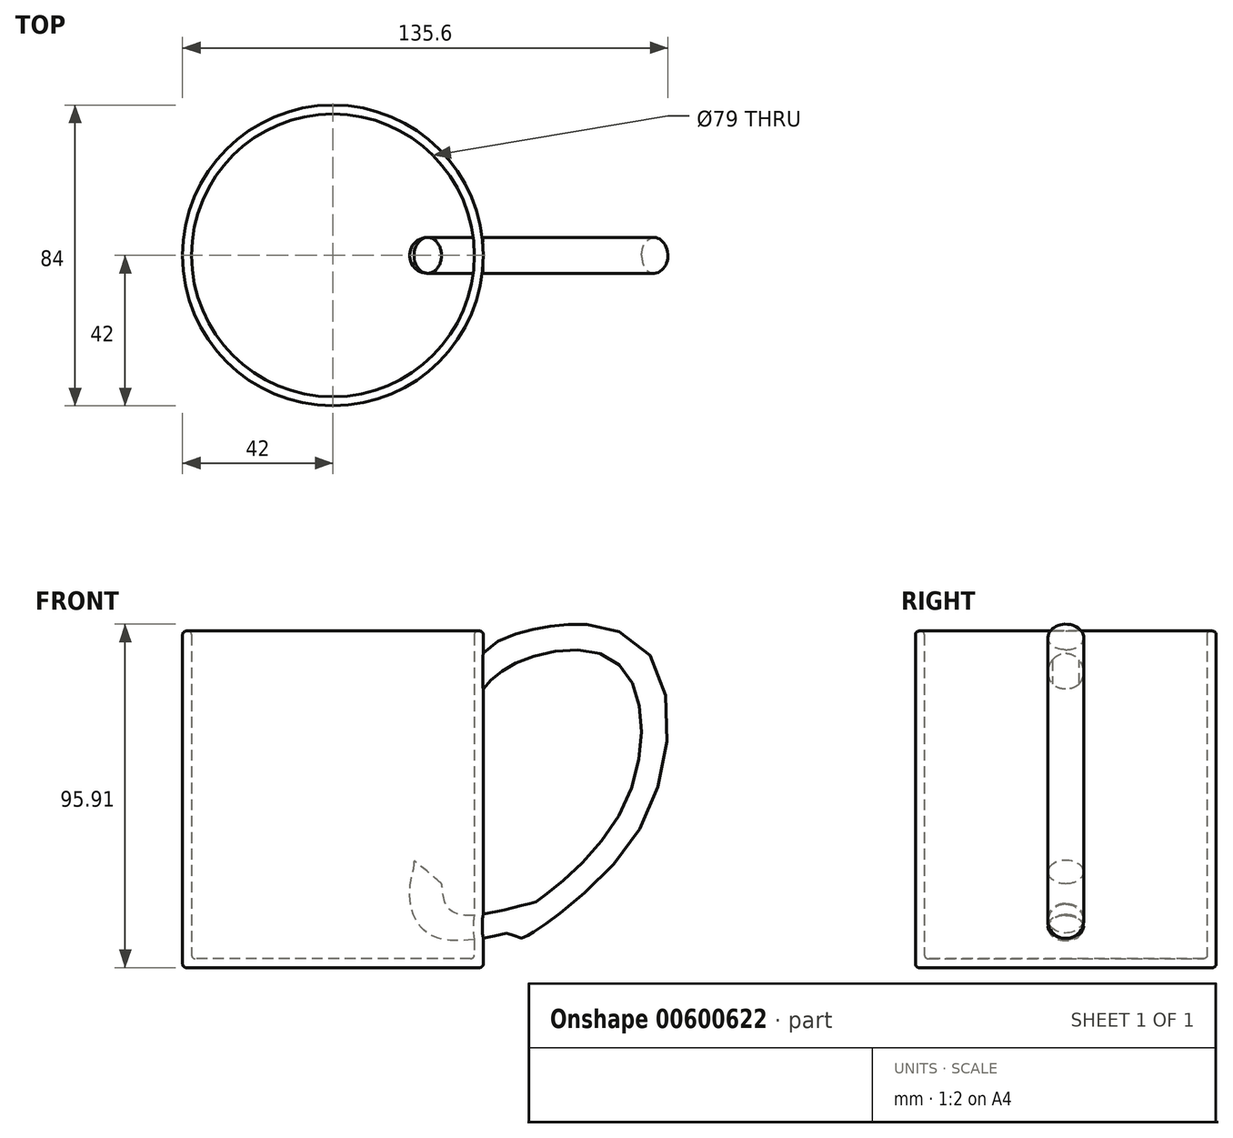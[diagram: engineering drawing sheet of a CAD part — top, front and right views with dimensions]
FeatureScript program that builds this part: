
annotation { "Feature Type Name" : "Feature", "Feature Type Description" : "" }
export const myFeature = defineFeature(function(context is Context, id is Id, definition is map)
    precondition{}
    {
        {
            var Q0;
            Q0=qCreatedBy(makeId("Top.planeOp"),FACE);
            var sketch = newSketch(context, id + "F0", { "sketchPlane" : qUnion([Q0])});
            skCircle(sketch, "E0", {"center": v(0, 0) * mm, "radius": 42 * mm});
            skSolve(sketch);
        }
        {
            var Q0;
            Q0=makeQuery(id+"F0.imprint","IMPRINT",FACE,{"disambiguationData":[TD([[makeQuery(id+"F0.imprint","IMPRINT",EDGE,{"derivedFrom":sQuery(id+"F0.wireOp",EDGE,"E0")}),1.0]])]});
            extrude(context, id + "F1", {"entities" : qUnion([Q0]), "depth" : 94 * mm, "offsetDistance" : 25 * mm});
        }
        {
            var Q0;
            Q0=qCreatedBy(makeId("Front.planeOp"),FACE);
            var sketch = newSketch(context, id + "F2", { "sketchPlane" : qUnion([Q0])});
            skFitSpline(sketch, "E1", {"points": [v(41.84, 74.68) * mm, v(50.86, 82.86) * mm, v(77.66, 84) * mm, v(79.07, 44.78) * mm, v(56.79, 20.52) * mm, v(56.22, 20.24) * mm, v(36.48, 16.57) * mm, v(32.53, 21.65) * mm], "startDerivative": vector(52.64, 69.94) * mm, "endDerivative": vector(-17.3, 75.52) * mm});
            skSolve(sketch);
        }
        {
            var Q0;
            Q0=makeQuery(id+"F1.opExtrude","CAP_FACE",FACE,{"disambiguationData":[OSD([sQuery(id+"F0.wireOp",EDGE,"E0")])],"isStart":false});
            shell(context, id + "F3", {"entities" : qUnion([Q0]), "thickness" : 2.5 * mm});
        }
        {
            var Q0;
            Q0=qCreatedBy(makeId("Right.planeOp"),FACE);
            cPlane(context, id + "F4", {"entities" : qUnion([Q0]), "cplaneType" : CPlaneType.OFFSET, "offset" : 42 * mm, "width" : 150 * mm, "height" : 150 * mm});
        }
        {
            var Q0;
            Q0=qCreatedBy(id+"F4.planeOp",FACE);
            var sketch = newSketch(context, id + "F5", { "sketchPlane" : qUnion([Q0])});
            skCircle(sketch, "E2", {"center": v(0, 82.78) * mm, "radius": 5 * mm});
            skSolve(sketch);
        }
        {
            var Q0;
            Q0=makeQuery(id+"F5.imprint","IMPRINT",FACE,{"disambiguationData":[TD([[makeQuery(id+"F5.imprint","IMPRINT",EDGE,{"derivedFrom":sQuery(id+"F5.wireOp",EDGE,"E2")}),1.0]])]});
            var Q1;
            Q1=sQuery(id+"F2.wireOp",EDGE,"E1");
            sweep(context, id + "F6", {"operationType" : NewBodyOperationType.ADD, "profiles" : qUnion([Q0]), "path" : qUnion([Q1])});
        }
        {
            var Q0;
            {var subQ0=sQuery(id+"F0.wireOp",EDGE,"E0");Q0=makeQuery(id+"F3.opShell","OFFSET_EDGE",EDGE,{"disambiguationData":[OSD([subQ0]),TDD([makeQuery(id+"F1.opExtrude","CAP_EDGE",EDGE,{"disambiguationData":[OSD([subQ0])],"isStart":false})])]});}
            var Q1;
            Q1=makeQuery(id+"F1.opExtrude","CAP_EDGE",EDGE,{"disambiguationData":[OSD([sQuery(id+"F0.wireOp",EDGE,"E0")])],"isStart":false});
            var Q2;
            Q2=makeQuery(id+"F1.opExtrude","CAP_EDGE",EDGE,{"disambiguationData":[OSD([sQuery(id+"F0.wireOp",EDGE,"E0")])],"isStart":true});
            var Q3;
            {var subQ0=sQuery(id+"F0.wireOp",EDGE,"E0");Q3=makeQuery(id+"F3.opShell","OFFSET_FACE",FACE,{"disambiguationData":[OSD([subQ0]),TDD([makeQuery(id+"F1.opExtrude","CAP_FACE",FACE,{"disambiguationData":[OSD([subQ0])],"isStart":true})])]});}
            fillet(context, id + "F7", {"entities" : qUnion([Q0, Q1, Q2, Q3]), "radius" : 1 * mm, "tangentPropagation" : true, "allowEdgeOverflow" : false});
        }
    });
